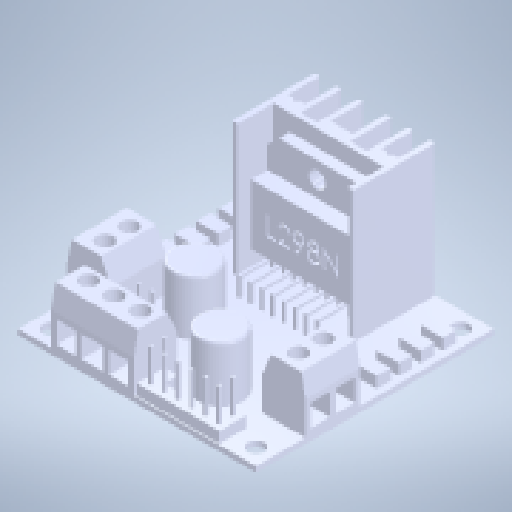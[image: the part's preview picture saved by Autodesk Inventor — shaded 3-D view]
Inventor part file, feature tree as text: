
AUTODESK INVENTOR PART (.ipt)
format: ipt  version: 2024 (Build 280153000, 153)  size: 490,496 bytes
history: native  units: in
note: dims shown in document units (in); Inventor stores cm internally (conversion verified against a paired STEP export)
features: fillet x1
ambient origin geometry x8: Origin, YZ Plane, XZ Plane, XY Plane, X Axis, Y Axis, Z Axis, Center Point
bodies: Solid1 (feature_tree)
feature tree (1):
  fillet  "Redondeo2"  [1 undecoded]
note: 1 required parameter value undecoded (feature->parameter linkage not recoverable at this tier; creation-order binding heuristic only, values carry confidence <= 0.55)
